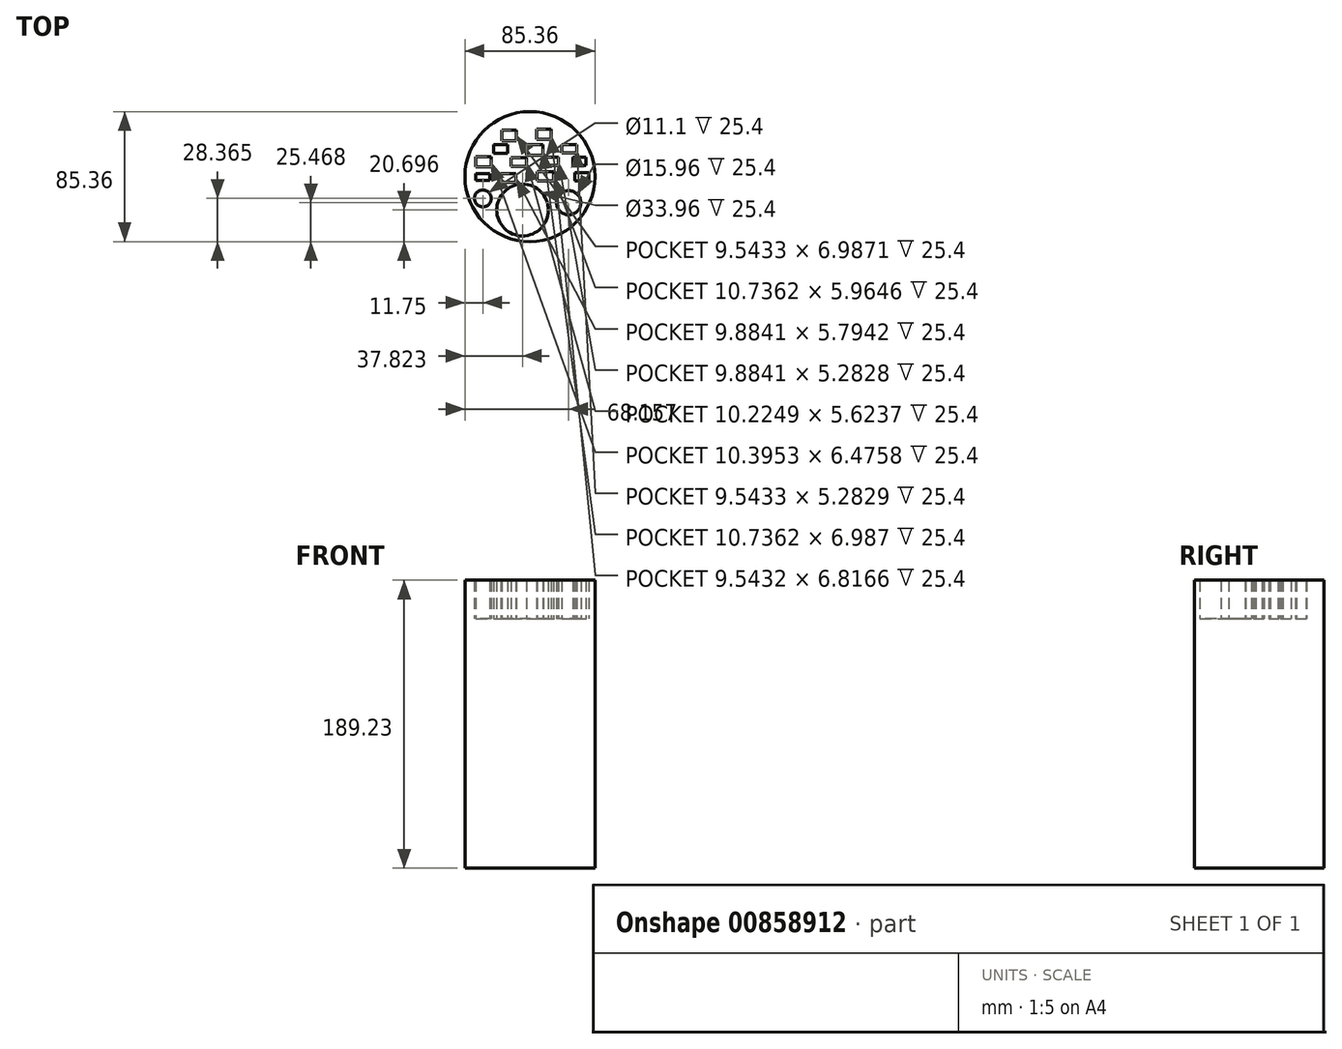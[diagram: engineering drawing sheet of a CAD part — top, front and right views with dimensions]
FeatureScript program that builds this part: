
annotation { "Feature Type Name" : "Feature", "Feature Type Description" : "" }
export const myFeature = defineFeature(function(context is Context, id is Id, definition is map)
    precondition{}
    {
        {
            var Q0;
            Q0=qCreatedBy(makeId("Top.planeOp"),FACE);
            var sketch = newSketch(context, id + "F0", { "sketchPlane" : qUnion([Q0])});
            skCircle(sketch, "E0", {"center": v(0, 0) * mm, "radius": 42.68 * mm});
            skSolve(sketch);
        }
        {
            var Q0;
            Q0 = qSketchRegion(id + "F0", true);
            extrude(context, id + "F1", {"entities" : qUnion([Q0]), "depth" : 163.83 * mm, "offsetDistance" : 25.4 * mm});
        }
        {
            var Q0;
            Q0=makeQuery(id+"F1.opExtrude","CAP_FACE",FACE,{"disambiguationData":[OSD([sQuery(id+"F0.wireOp",EDGE,"E0")])],"isStart":false});
            var sketch = newSketch(context, id + "F2", { "sketchPlane" : qUnion([Q0])});
            skLineSegment(sketch, "E1.bottom", {"start": v(-18.5, 23.69) * mm, "end": v(-8.95, 23.69) * mm});
            skLineSegment(sketch, "E1.top", {"start": v(-18.5, 30.67) * mm, "end": v(-8.95, 30.67) * mm});
            skLineSegment(sketch, "E1.left", {"start": v(-18.5, 23.69) * mm, "end": v(-18.5, 30.67) * mm});
            skLineSegment(sketch, "E1.right", {"start": v(-8.95, 23.69) * mm, "end": v(-8.95, 30.67) * mm});
            skLineSegment(sketch, "E2.bottom", {"start": v(4.35, 24.37) * mm, "end": v(13.89, 24.37) * mm});
            skLineSegment(sketch, "E2.top", {"start": v(4.35, 31.19) * mm, "end": v(13.89, 31.19) * mm});
            skLineSegment(sketch, "E2.left", {"start": v(4.35, 24.37) * mm, "end": v(4.35, 31.19) * mm});
            skLineSegment(sketch, "E2.right", {"start": v(13.89, 24.37) * mm, "end": v(13.89, 31.19) * mm});
            skLineSegment(sketch, "E3.bottom", {"start": v(-2.3, 13.97) * mm, "end": v(8.44, 13.97) * mm});
            skLineSegment(sketch, "E3.top", {"start": v(-2.3, 20.96) * mm, "end": v(8.44, 20.96) * mm});
            skLineSegment(sketch, "E3.left", {"start": v(-2.3, 13.97) * mm, "end": v(-2.3, 20.96) * mm});
            skLineSegment(sketch, "E3.right", {"start": v(8.44, 13.97) * mm, "end": v(8.44, 20.96) * mm});
            skLineSegment(sketch, "E4.bottom", {"start": v(-23.77, 15.34) * mm, "end": v(-14.74, 15.34) * mm});
            skLineSegment(sketch, "E4.top", {"start": v(-23.77, 20.96) * mm, "end": v(-14.74, 20.96) * mm});
            skLineSegment(sketch, "E4.left", {"start": v(-23.77, 15.34) * mm, "end": v(-23.77, 20.96) * mm});
            skLineSegment(sketch, "E4.right", {"start": v(-14.74, 15.34) * mm, "end": v(-14.74, 20.96) * mm});
            skLineSegment(sketch, "E5.bottom", {"start": v(21.05, 15.68) * mm, "end": v(30.59, 15.68) * mm});
            skLineSegment(sketch, "E5.top", {"start": v(21.05, 20.96) * mm, "end": v(30.59, 20.96) * mm});
            skLineSegment(sketch, "E5.left", {"start": v(21.05, 15.68) * mm, "end": v(21.05, 20.96) * mm});
            skLineSegment(sketch, "E5.right", {"start": v(30.59, 15.68) * mm, "end": v(30.59, 20.96) * mm});
            skLineSegment(sketch, "E6.bottom", {"start": v(-35.7, 6.48) * mm, "end": v(-25.3, 6.48) * mm});
            skLineSegment(sketch, "E6.top", {"start": v(-35.7, 12.95) * mm, "end": v(-25.3, 12.95) * mm});
            skLineSegment(sketch, "E6.left", {"start": v(-35.7, 6.48) * mm, "end": v(-35.7, 12.95) * mm});
            skLineSegment(sketch, "E6.right", {"start": v(-25.3, 6.48) * mm, "end": v(-25.3, 12.95) * mm});
            skLineSegment(sketch, "E7.bottom", {"start": v(-12.53, 6.65) * mm, "end": v(-2.3, 6.65) * mm});
            skLineSegment(sketch, "E7.top", {"start": v(-12.53, 12.27) * mm, "end": v(-2.3, 12.27) * mm});
            skLineSegment(sketch, "E7.left", {"start": v(-12.53, 6.65) * mm, "end": v(-12.53, 12.27) * mm});
            skLineSegment(sketch, "E7.right", {"start": v(-2.3, 6.65) * mm, "end": v(-2.3, 12.27) * mm});
            skLineSegment(sketch, "E8.bottom", {"start": v(8.78, 7.33) * mm, "end": v(18.66, 7.33) * mm});
            skLineSegment(sketch, "E8.top", {"start": v(8.78, 12.61) * mm, "end": v(18.66, 12.61) * mm});
            skLineSegment(sketch, "E8.left", {"start": v(8.78, 7.33) * mm, "end": v(8.78, 12.61) * mm});
            skLineSegment(sketch, "E8.right", {"start": v(18.66, 7.33) * mm, "end": v(18.66, 12.61) * mm});
            skLineSegment(sketch, "E9.bottom", {"start": v(28.2, 7.33) * mm, "end": v(36.72, 7.33) * mm});
            skLineSegment(sketch, "E9.top", {"start": v(28.2, 12.61) * mm, "end": v(36.72, 12.61) * mm});
            skLineSegment(sketch, "E9.left", {"start": v(28.2, 7.33) * mm, "end": v(28.2, 12.61) * mm});
            skLineSegment(sketch, "E9.right", {"start": v(36.72, 7.33) * mm, "end": v(36.72, 12.61) * mm});
            skLineSegment(sketch, "E10.bottom", {"start": v(-19.17, -3.92) * mm, "end": v(-9.29, -3.92) * mm});
            skLineSegment(sketch, "E10.top", {"start": v(-19.17, 1.87) * mm, "end": v(-9.29, 1.87) * mm});
            skLineSegment(sketch, "E10.left", {"start": v(-19.17, -3.92) * mm, "end": v(-19.17, 1.87) * mm});
            skLineSegment(sketch, "E10.right", {"start": v(-9.29, -3.92) * mm, "end": v(-9.29, 1.87) * mm});
            skLineSegment(sketch, "E11.bottom", {"start": v(4.69, -2.9) * mm, "end": v(15.42, -2.9) * mm});
            skLineSegment(sketch, "E11.top", {"start": v(4.69, 3.07) * mm, "end": v(15.42, 3.07) * mm});
            skLineSegment(sketch, "E11.left", {"start": v(4.69, -2.9) * mm, "end": v(4.69, 3.07) * mm});
            skLineSegment(sketch, "E11.right", {"start": v(15.42, -2.9) * mm, "end": v(15.42, 3.07) * mm});
            skLineSegment(sketch, "E12.bottom", {"start": v(29.57, -2.9) * mm, "end": v(38.6, -2.9) * mm});
            skLineSegment(sketch, "E12.top", {"start": v(29.57, 2.56) * mm, "end": v(38.6, 2.56) * mm});
            skLineSegment(sketch, "E12.left", {"start": v(29.57, -2.9) * mm, "end": v(29.57, 2.56) * mm});
            skLineSegment(sketch, "E12.right", {"start": v(38.6, -2.9) * mm, "end": v(38.6, 2.56) * mm});
            skLineSegment(sketch, "E13.bottom", {"start": v(-35.53, -2.39) * mm, "end": v(-26.5, -2.39) * mm});
            skLineSegment(sketch, "E13.top", {"start": v(-35.53, 1.87) * mm, "end": v(-26.5, 1.87) * mm});
            skLineSegment(sketch, "E13.left", {"start": v(-35.53, -2.39) * mm, "end": v(-35.53, 1.87) * mm});
            skLineSegment(sketch, "E13.right", {"start": v(-26.5, -2.39) * mm, "end": v(-26.5, 1.87) * mm});
            skCircle(sketch, "E14", {"center": v(-4.86, -21.98) * mm, "radius": 16.98 * mm});
            skCircle(sketch, "E15", {"center": v(25.48, -17.21) * mm, "radius": 7.98 * mm});
            skCircle(sketch, "E16", {"center": v(-30.93, -14.31) * mm, "radius": 5.55 * mm});
            skSolve(sketch);
        }
        {
            var Q0;
            Q0=makeQuery(id+"F2.imprint","IMPRINT",FACE,{"disambiguationData":[TD([[makeQuery(id+"F2.imprint","IMPRINT",EDGE,{"derivedFrom":sQuery(id+"F2.wireOp",EDGE,"E1.bottom")}),-1.0]])]});
            extrude(context, id + "F3", {"entities" : qUnion([Q0]), "operationType" : NewBodyOperationType.ADD, "depth" : 25.4 * mm, "offsetDistance" : 25.4 * mm});
        }
    });
